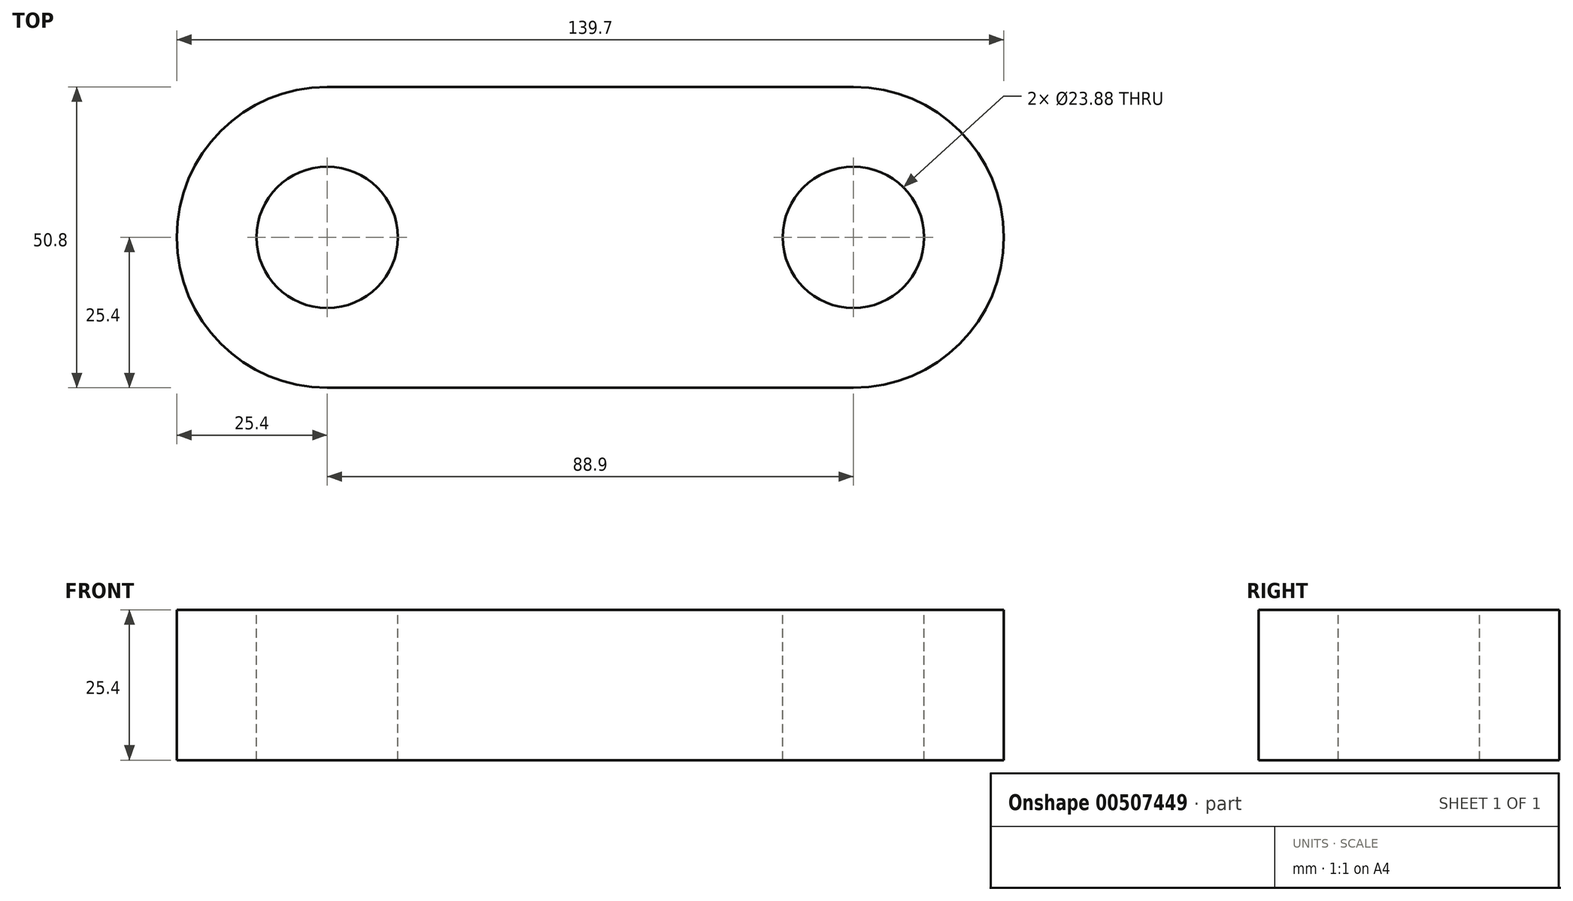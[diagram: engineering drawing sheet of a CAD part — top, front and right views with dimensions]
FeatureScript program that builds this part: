
annotation { "Feature Type Name" : "Feature", "Feature Type Description" : "" }
export const myFeature = defineFeature(function(context is Context, id is Id, definition is map)
    precondition{}
    {
        {
            var Q0;
            Q0=qCreatedBy(makeId("Top.planeOp"),FACE);
            var sketch = newSketch(context, id + "F0", { "sketchPlane" : qUnion([Q0])});
            skLineSegment(sketch, "E0.bottom", {"start": v(-44.45, 25.4) * mm, "end": v(44.45, 25.4) * mm});
            skLineSegment(sketch, "E0.top", {"start": v(-44.45, -25.4) * mm, "end": v(44.45, -25.4) * mm});
            skLineSegment(sketch, "E0.left", {"start": v(-44.45, 25.4) * mm, "end": v(-44.45, -25.4) * mm, "construction": true});
            skLineSegment(sketch, "E0.right", {"start": v(44.45, 25.4) * mm, "end": v(44.45, -25.4) * mm, "construction": true});
            skPoint(sketch, "E0.middle", {"position": v(0, 0) * mm});
            skArc(sketch, "E1", {"start": v(-44.45, 25.4) * mm, "mid": v(-69.85, 0) * mm, "end": v(-44.45, -25.4) * mm});
            skArc(sketch, "E2", {"start": v(44.45, -25.4) * mm, "mid": v(69.85, 0) * mm, "end": v(44.45, 25.4) * mm});
            skCircle(sketch, "E3", {"center": v(44.45, 0) * mm, "radius": 11.94 * mm});
            skCircle(sketch, "E4", {"center": v(44.45, 0) * mm, "radius": 6.74 * mm});
            skCircle(sketch, "E5", {"center": v(-44.45, 0) * mm, "radius": 11.94 * mm});
            skCircle(sketch, "E6", {"center": v(-44.45, 0) * mm, "radius": 6.74 * mm});
            skSolve(sketch);
        }
        {
            var Q0;
            Q0=makeQuery(id+"F0.imprint","IMPRINT",FACE,{"disambiguationData":[TD([[makeQuery(id+"F0.imprint","IMPRINT",EDGE,{"derivedFrom":sQuery(id+"F0.wireOp",EDGE,"E0.bottom")}),-1.0]])]});
            extrude(context, id + "F1", {"entities" : qUnion([Q0]), "oppositeDirection" : true, "depth" : 25.4 * mm});
        }
    });
